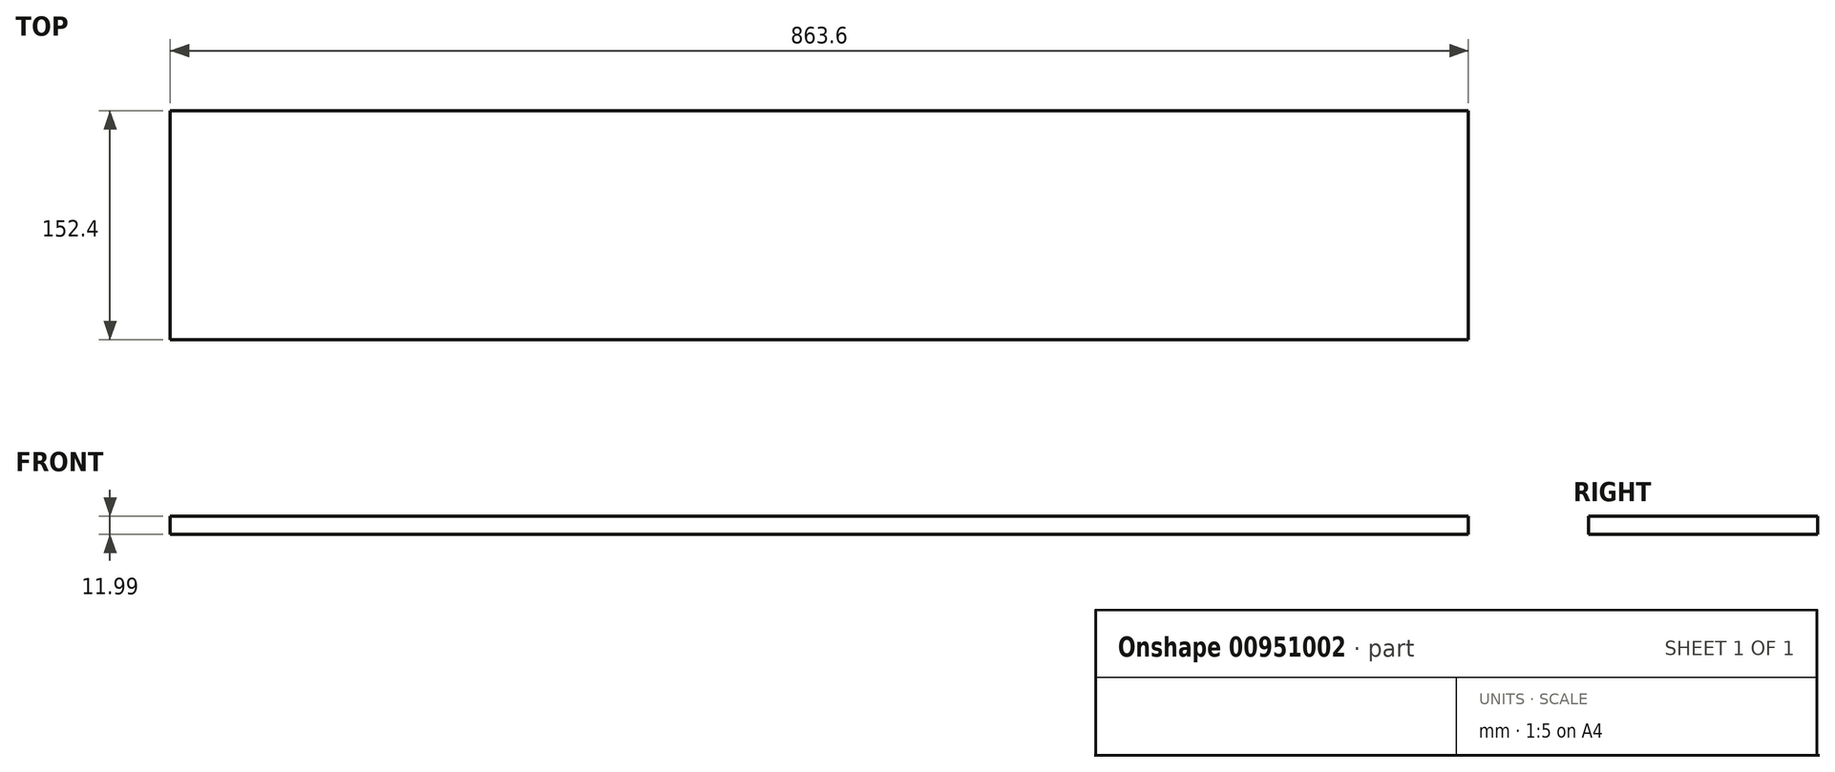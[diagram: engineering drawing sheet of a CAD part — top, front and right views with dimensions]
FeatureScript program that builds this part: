
annotation { "Feature Type Name" : "Feature", "Feature Type Description" : "" }
export const myFeature = defineFeature(function(context is Context, id is Id, definition is map)
    precondition{}
    {
        {
            var Q0;
            Q0=qCreatedBy(makeId("Top.planeOp"),FACE);
            var sketch = newSketch(context, id + "F0", { "sketchPlane" : qUnion([Q0])});
            skLineSegment(sketch, "E0.bottom", {"start": v(431.8, 76.2) * mm, "end": v(-431.8, 76.2) * mm});
            skLineSegment(sketch, "E0.top", {"start": v(431.8, -76.2) * mm, "end": v(-431.8, -76.2) * mm});
            skLineSegment(sketch, "E0.left", {"start": v(431.8, 76.2) * mm, "end": v(431.8, -76.2) * mm});
            skLineSegment(sketch, "E0.right", {"start": v(-431.8, 76.2) * mm, "end": v(-431.8, -76.2) * mm});
            skPoint(sketch, "E0.middle", {"position": v(0, 0) * mm});
            skSolve(sketch);
        }
        {
            var Q0;
            Q0 = qSketchRegion(id + "F0", true);
            extrude(context, id + "F1", {"entities" : qUnion([Q0]), "depth" : 12 * mm, "offsetDistance" : 25.4 * mm});
        }
    });
